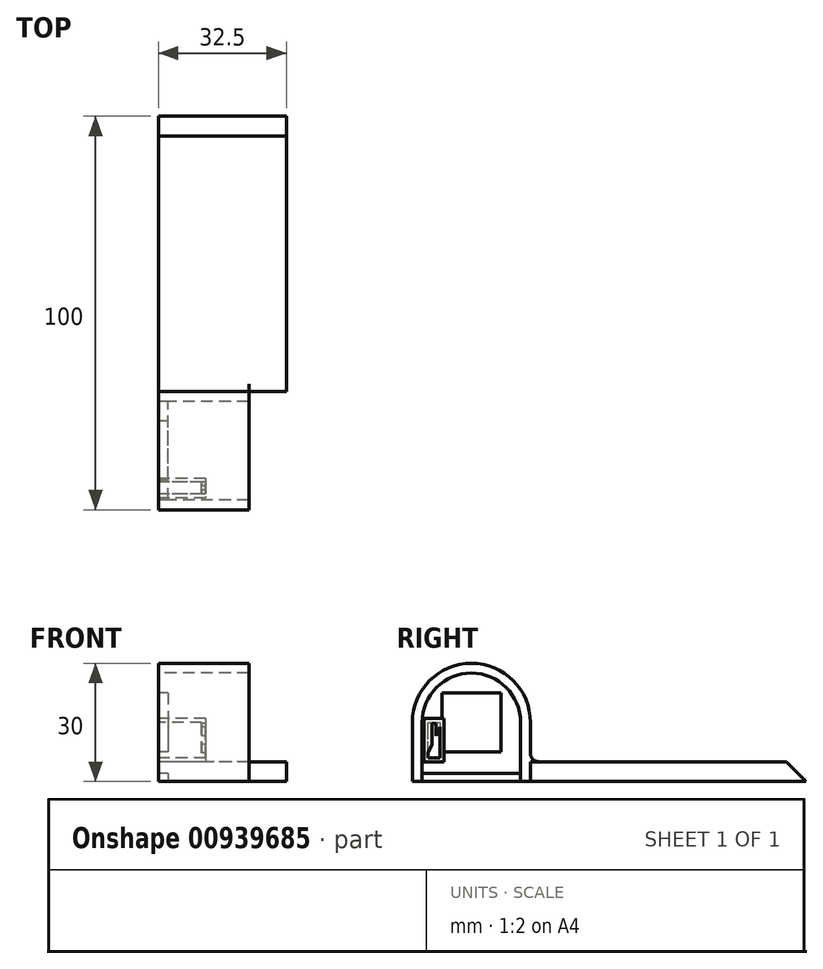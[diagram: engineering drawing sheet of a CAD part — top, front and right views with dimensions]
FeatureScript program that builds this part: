
annotation { "Feature Type Name" : "Feature", "Feature Type Description" : "" }
export const myFeature = defineFeature(function(context is Context, id is Id, definition is map)
    precondition{}
    {
        {
            var Q0;
            Q0=qCreatedBy(makeId("Right.planeOp"),FACE);
            cPlane(context, id + "F0", {"entities" : qUnion([Q0]), "cplaneType" : CPlaneType.OFFSET, "offset" : 27.5 * mm, "oppositeDirection" : true, "width" : 150 * mm, "height" : 150 * mm});
        }
        {
            var Q0;
            Q0=qCreatedBy(id+"F0.planeOp",FACE);
            var sketch = newSketch(context, id + "F1", { "sketchPlane" : qUnion([Q0])});
            skLineSegment(sketch, "E0.bottom", {"start": v(0, 0) * mm, "end": v(-30, 0) * mm});
            skLineSegment(sketch, "E1", {"start": v(-30, 0) * mm, "end": v(-30, 15) * mm});
            skLineSegment(sketch, "E2", {"start": v(0, 0) * mm, "end": v(0, 15) * mm});
            skArc(sketch, "E3", {"start": v(0, 15) * mm, "mid": v(-15, 30) * mm, "end": v(-30, 15) * mm});
            skLineSegment(sketch, "E4", {"start": v(-2.5, 15) * mm, "end": v(-2.5, 0) * mm});
            skLineSegment(sketch, "E5", {"start": v(-27.5, 15) * mm, "end": v(-27.5, 0) * mm});
            skArc(sketch, "E6", {"start": v(-2.5, 15) * mm, "mid": v(-15, 27.5) * mm, "end": v(-27.5, 15) * mm});
            skLineSegment(sketch, "E7", {"start": v(-27.5, 0) * mm, "end": v(-27.5, 2) * mm});
            skLineSegment(sketch, "E8", {"start": v(-26, 15) * mm, "end": v(-23, 15) * mm});
            skLineSegment(sketch, "E9", {"start": v(-23, 15) * mm, "end": v(-23, 6) * mm});
            skLineSegment(sketch, "E10", {"start": v(-23, 6) * mm, "end": v(-26, 6) * mm});
            skLineSegment(sketch, "E11", {"start": v(-26, 6) * mm, "end": v(-26, 15) * mm});
            skLineSegment(sketch, "E12", {"start": v(-26, 15) * mm, "end": v(-27, 15) * mm});
            skLineSegment(sketch, "E13", {"start": v(-27, 15) * mm, "end": v(-27, 16) * mm});
            skLineSegment(sketch, "E14.bottom", {"start": v(-27, 16) * mm, "end": v(-22, 16) * mm});
            skLineSegment(sketch, "E14.top", {"start": v(-27, 5) * mm, "end": v(-22, 5) * mm});
            skLineSegment(sketch, "E14.left", {"start": v(-27, 16) * mm, "end": v(-27, 5) * mm});
            skLineSegment(sketch, "E14.right", {"start": v(-22, 16) * mm, "end": v(-22, 5) * mm});
            skPoint(sketch, "E14.middle", {"position": v(-24.5, 10.5) * mm});
            skLineSegment(sketch, "E15", {"start": v(-23, 15) * mm, "end": v(-15, 15) * mm});
            skLineSegment(sketch, "E16.bottom", {"start": v(-22.5, 22.5) * mm, "end": v(-7.5, 22.5) * mm});
            skLineSegment(sketch, "E16.top", {"start": v(-22.5, 7.5) * mm, "end": v(-7.5, 7.5) * mm});
            skLineSegment(sketch, "E16.left", {"start": v(-22.5, 22.5) * mm, "end": v(-22.5, 7.5) * mm});
            skLineSegment(sketch, "E16.right", {"start": v(-7.5, 22.5) * mm, "end": v(-7.5, 7.5) * mm});
            skLineSegment(sketch, "E17", {"start": v(-30, 0) * mm, "end": v(70, 0) * mm});
            skLineSegment(sketch, "E18", {"start": v(70, 0) * mm, "end": v(70, 5) * mm});
            skLineSegment(sketch, "E19", {"start": v(70, 5) * mm, "end": v(0, 5) * mm});
            skLineSegment(sketch, "E20", {"start": v(-27.5, 0) * mm, "end": v(-30, 0) * mm});
            skLineSegment(sketch, "E21", {"start": v(-27.5, 2) * mm, "end": v(-2.5, 2) * mm});
            skSolve(sketch);
        }
        {
            var Q0;
            {var subQ2=sQuery(id+"F1.wireOp",EDGE,"E9");Q0=makeQuery(id+"F1.imprint","IMPRINT",FACE,{"disambiguationData":[TD([[makeQuery(id+"F1.imprint","IMPRINT",EDGE,{"derivedFrom":subQ2}),1.0]])]});}
            var Q1;
            {var subQ8=sQuery(id+"F1.wireOp",EDGE,"E8");Q1=makeQuery(id+"F1.imprint","IMPRINT",FACE,{"disambiguationData":[TD([[makeQuery(id+"F1.imprint","IMPRINT",EDGE,{"derivedFrom":subQ8}),1.0]])]});}
            var Q2;
            {var subQ0=sQuery(id+"F1.wireOp",EDGE,"E15");var subQ1=sQuery(id+"F1.wireOp",EDGE,"E14.right");var subQ2=makeQuery(id+"F1.imprint","INTERSECT",VERTEX,{"derivedFrom":[subQ1,subQ0]});Q2=makeQuery(id+"F1.imprint","IMPRINT",FACE,{"disambiguationData":[TD([[makeQuery(id+"F1.imprint","IMPRINT",EDGE,{"disambiguationData":[TD([[subQ2,-1.0]])],"derivedFrom":subQ1}),-1.0]])]});}
            var Q3;
            {var subQ0=sQuery(id+"F1.wireOp",EDGE,"E14.right");var subQ1=sQuery(id+"F1.wireOp",EDGE,"E14.bottom");var subQ2=makeQuery(id+"F1.imprint","INTERSECT",VERTEX,{"derivedFrom":[subQ1,subQ0]});Q3=makeQuery(id+"F1.imprint","IMPRINT",FACE,{"disambiguationData":[TD([[makeQuery(id+"F1.imprint","IMPRINT",EDGE,{"disambiguationData":[TD([[subQ2,1.0]])],"derivedFrom":subQ1}),-1.0]])]});}
            extrude(context, id + "F2", {"entities" : qUnion([Q0, Q1, Q2, Q3]), "depth" : 11 * mm, "offsetDistance" : 25 * mm});
        }
        {
            var Q0;
            {var subQ10=sQuery(id+"F1.wireOp",EDGE,"E4");Q0=makeQuery(id+"F1.imprint","IMPRINT",FACE,{"disambiguationData":[TD([[makeQuery(id+"F1.imprint","IMPRINT",EDGE,{"derivedFrom":subQ10}),-1.0]])]});}
            var Q1;
            {var subQ0=sQuery(id+"F1.wireOp",EDGE,"E16.bottom");Q1=makeQuery(id+"F1.imprint","IMPRINT",FACE,{"disambiguationData":[TD([[makeQuery(id+"F1.imprint","IMPRINT",EDGE,{"derivedFrom":subQ0}),-1.0]])]});}
            var Q2;
            Q2=makeQuery(id+"F1.imprint","IMPRINT",FACE,{"disambiguationData":[TD([[makeQuery(id+"F1.imprint","IMPRINT",EDGE,{"derivedFrom":sQuery(id+"F1.wireOp",EDGE,"E5")}),1.0]])]});
            extrude(context, id + "F3", {"entities" : qUnion([Q0, Q1, Q2]), "operationType" : NewBodyOperationType.ADD, "depth" : 2.5 * mm, "offsetDistance" : 25 * mm});
        }
        {
            var Q0;
            Q0=qCreatedBy(makeId("Right.planeOp"),FACE);
            cPlane(context, id + "F4", {"entities" : qUnion([Q0]), "cplaneType" : CPlaneType.OFFSET, "offset" : 16.5 * mm, "oppositeDirection" : true, "width" : 150 * mm, "height" : 150 * mm});
        }
        {
            var Q0;
            Q0=qCreatedBy(id+"F4.planeOp",FACE);
            var sketch = newSketch(context, id + "F5", { "sketchPlane" : qUnion([Q0])});
            skLineSegment(sketch, "E22.0.0", {"start": v(-26, 15) * mm, "end": v(-26, 6) * mm});
            skLineSegment(sketch, "E22.0.1", {"start": v(-26, 6) * mm, "end": v(-23, 6) * mm});
            skLineSegment(sketch, "E22.0.2", {"start": v(-23, 6) * mm, "end": v(-23, 15) * mm});
            skLineSegment(sketch, "E22.0.3", {"start": v(-23, 15) * mm, "end": v(-26, 15) * mm});
            skLineSegment(sketch, "E23.0.0", {"start": v(-22, 16) * mm, "end": v(-27, 16) * mm});
            skLineSegment(sketch, "E23.0.1", {"start": v(-27, 16) * mm, "end": v(-27, 5) * mm});
            skLineSegment(sketch, "E23.0.2", {"start": v(-27, 5) * mm, "end": v(-22, 5) * mm});
            skLineSegment(sketch, "E23.0.3", {"start": v(-22, 5) * mm, "end": v(-22, 16) * mm});
            skLineSegment(sketch, "E24", {"start": v(-26, 15) * mm, "end": v(-26, 14) * mm});
            skLineSegment(sketch, "E25.top", {"start": v(-25, 5) * mm, "end": v(-24, 5) * mm});
            skPoint(sketch, "E25.middle", {"position": v(-24.5, 9.5) * mm});
            skLineSegment(sketch, "E26", {"start": v(-22, 16) * mm, "end": v(-27, 5) * mm});
            skLineSegment(sketch, "E27.bottom", {"start": v(-25, 14.75) * mm, "end": v(-24, 14.75) * mm});
            skLineSegment(sketch, "E27.top", {"start": v(-25, 6.25) * mm, "end": v(-24, 6.25) * mm});
            skLineSegment(sketch, "E27.left", {"start": v(-25, 14.75) * mm, "end": v(-25, 6.25) * mm});
            skLineSegment(sketch, "E27.right", {"start": v(-24, 14.75) * mm, "end": v(-24, 6.25) * mm});
            skPoint(sketch, "E27.middle", {"position": v(-24.5, 10.5) * mm});
            skSolve(sketch);
        }
        {
            var Q0;
            Q0 = qSketchRegion(id + "F5", true);
            var Q1;
            Q1=makeQuery(id+"F5.imprint","IMPRINT",FACE,{"disambiguationData":[TD([[makeQuery(id+"F5.imprint","IMPRINT",EDGE,{"derivedFrom":sQuery(id+"F5.wireOp",EDGE,"E22.0.0")}),1.0]])]});
            var Q2;
            {var subQ7=sQuery(id+"F5.wireOp",EDGE,"E22.0.3");Q2=makeQuery(id+"F5.imprint","IMPRINT",FACE,{"disambiguationData":[TD([[makeQuery(id+"F5.imprint","IMPRINT",EDGE,{"derivedFrom":subQ7}),1.0]])]});}
            extrude(context, id + "F6", {"entities" : qUnion([Q0, Q1, Q2]), "operationType" : NewBodyOperationType.ADD, "depth" : 1 * mm, "offsetDistance" : 25 * mm});
        }
        {
            var Q0;
            Q0=makeQuery(id+"F1.imprint","IMPRINT",FACE,{"disambiguationData":[TD([[makeQuery(id+"F1.imprint","IMPRINT",EDGE,{"derivedFrom":sQuery(id+"F1.wireOp",EDGE,"E1")}),-1.0]])]});
            var Q1;
            {var subQ4=sQuery(id+"F1.wireOp",EDGE,"E18");Q1=makeQuery(id+"F1.imprint","IMPRINT",FACE,{"disambiguationData":[TD([[makeQuery(id+"F1.imprint","IMPRINT",EDGE,{"derivedFrom":subQ4}),1.0]])]});}
            var Q2;
            {var subQ4=sQuery(id+"F1.wireOp",EDGE,"E7");Q2=makeQuery(id+"F1.imprint","IMPRINT",FACE,{"disambiguationData":[TD([[makeQuery(id+"F1.imprint","IMPRINT",EDGE,{"derivedFrom":subQ4}),-1.0]])]});}
            extrude(context, id + "F7", {"entities" : qUnion([Q0, Q1, Q2]), "operationType" : NewBodyOperationType.ADD, "depth" : 23 * mm, "offsetDistance" : 25 * mm});
        }
        {
            var Q0;
            Q0=qCreatedBy(id+"F0.planeOp",FACE);
            cPlane(context, id + "F8", {"entities" : qUnion([Q0]), "cplaneType" : CPlaneType.OFFSET, "offset" : 20 * mm, "width" : 150 * mm, "height" : 150 * mm});
        }
        {
            var Q0;
            Q0=qCreatedBy(id+"F8.planeOp",FACE);
            var sketch = newSketch(context, id + "F9", { "sketchPlane" : qUnion([Q0])});
            skLineSegment(sketch, "E28.0.0", {"start": v(70, 0) * mm, "end": v(70, 5) * mm});
            skLineSegment(sketch, "E28.0.1", {"start": v(70, 5) * mm, "end": v(0, 5) * mm});
            skLineSegment(sketch, "E28.0.2", {"start": v(0, 5) * mm, "end": v(0, 0) * mm});
            skLineSegment(sketch, "E28.0.3", {"start": v(0, 0) * mm, "end": v(70, 0) * mm});
            skSolve(sketch);
        }
        {
            var Q0;
            Q0=makeQuery(id+"F9.imprint","IMPRINT",FACE,{"disambiguationData":[TD([[makeQuery(id+"F9.imprint","IMPRINT",EDGE,{"derivedFrom":sQuery(id+"F9.wireOp",EDGE,"E28.0.0")}),1.0]])]});
            extrude(context, id + "F10", {"entities" : qUnion([Q0]), "operationType" : NewBodyOperationType.ADD, "depth" : 12.5 * mm, "offsetDistance" : 25 * mm});
        }
        {
            var Q0;
            Q0=makeQuery(id+"F7.opExtrude","SWEPT_EDGE",EDGE,{"disambiguationData":[OSD([sQuery(id+"F1.wireOp",EDGE,"E18"),sQuery(id+"F1.wireOp",EDGE,"E19")])]});
            chamfer(context, id + "F11", {"entities" : qUnion([Q0]), "width" : 5 * mm, "tangentPropagation" : true});
        }
        {
            var Q0;
            Q0=qCreatedBy(id+"F0.planeOp",FACE);
            cPlane(context, id + "F12", {"entities" : qUnion([Q0]), "cplaneType" : CPlaneType.OFFSET, "offset" : 23 * mm, "width" : 150 * mm, "height" : 150 * mm});
        }
        {
            var Q0;
            Q0=makeQuery(id+"F7.opExtrude","SWEPT_EDGE",EDGE,{"disambiguationData":[OSD([sQuery(id+"F1.wireOp",EDGE,"E2"),sQuery(id+"F1.wireOp",EDGE,"E19")])]});
            fillet(context, id + "F13", {"entities" : qUnion([Q0]), "radius" : 2 * mm, "tangentPropagation" : true, "allowEdgeOverflow" : false});
        }
    });
